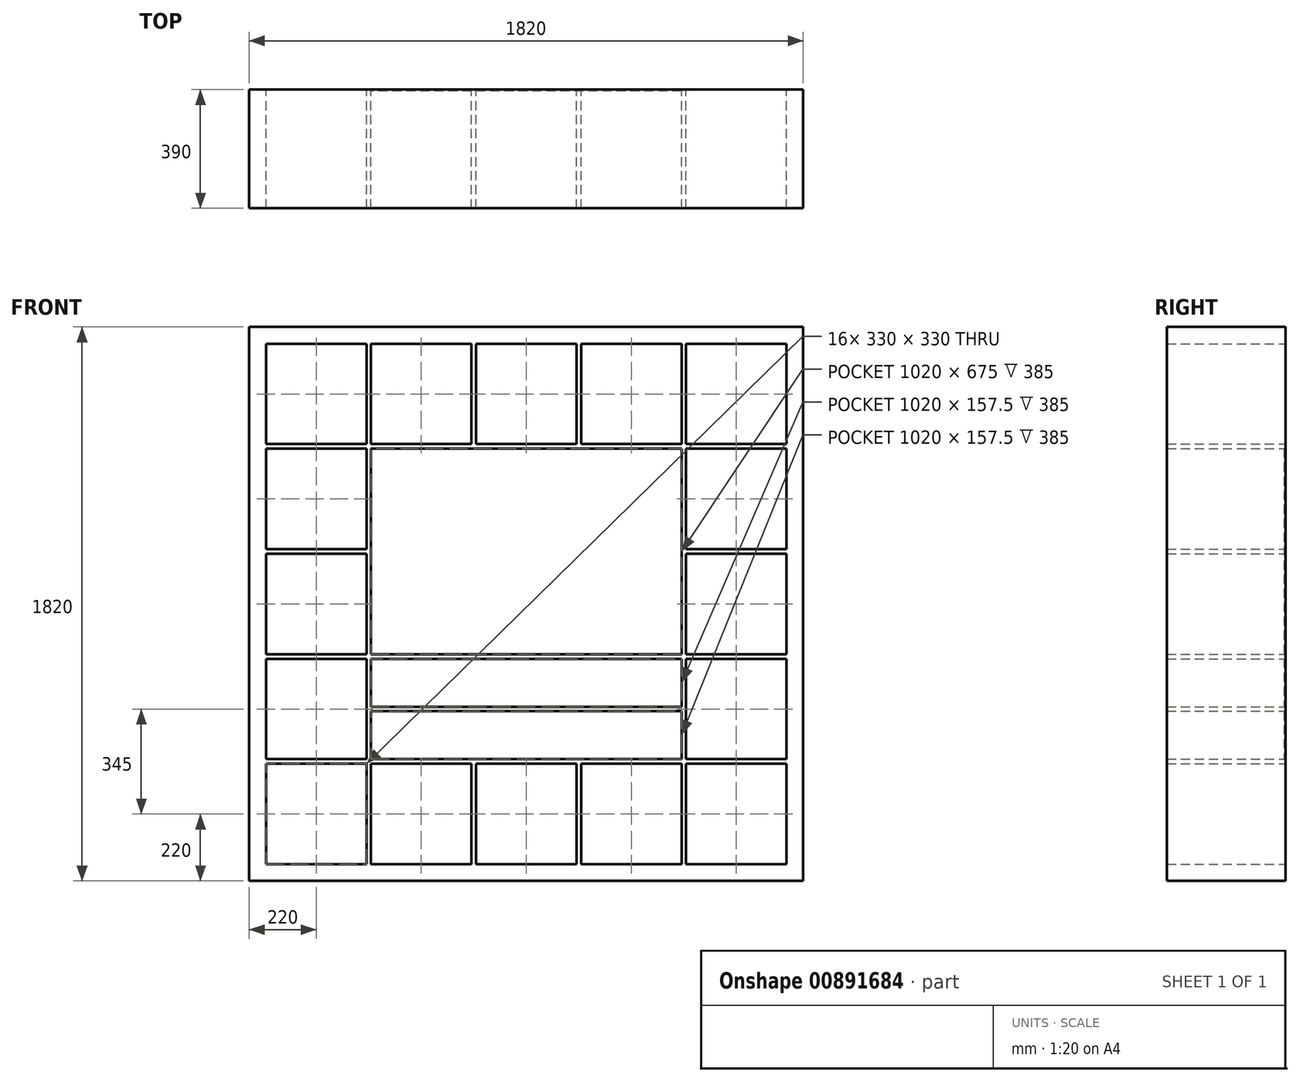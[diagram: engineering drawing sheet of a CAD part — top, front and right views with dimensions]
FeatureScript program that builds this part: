
annotation { "Feature Type Name" : "Feature", "Feature Type Description" : "" }
export const myFeature = defineFeature(function(context is Context, id is Id, definition is map)
    precondition{}
    {
        {
            var Q0;
            Q0=qCreatedBy(makeId("Front.planeOp"),FACE);
            var sketch = newSketch(context, id + "F0", { "sketchPlane" : qUnion([Q0])});
            skLineSegment(sketch, "E0.bottom", {"start": v(0, 1820) * mm, "end": v(1820, 1820) * mm});
            skLineSegment(sketch, "E0.top", {"start": v(0, 0) * mm, "end": v(1820, 0) * mm});
            skLineSegment(sketch, "E0.left", {"start": v(0, 1820) * mm, "end": v(0, 0) * mm});
            skLineSegment(sketch, "E0.right", {"start": v(1820, 1820) * mm, "end": v(1820, 0) * mm});
            skSolve(sketch);
        }
        {
            var Q0;
            Q0=makeQuery(id+"F0.imprint","IMPRINT",FACE,{"disambiguationData":[TD([[makeQuery(id+"F0.imprint","IMPRINT",EDGE,{"derivedFrom":sQuery(id+"F0.wireOp",EDGE,"E0.bottom")}),-1.0]])]});
            extrude(context, id + "F1", {"entities" : qUnion([Q0]), "depth" : 390 * mm});
        }
        {
            var Q0;
            Q0=qCreatedBy(makeId("Front.planeOp"),FACE);
            var sketch = newSketch(context, id + "F2", { "sketchPlane" : qUnion([Q0])});
            skLineSegment(sketch, "E1.bottom", {"start": v(385, 385) * mm, "end": v(55, 385) * mm});
            skLineSegment(sketch, "E1.top", {"start": v(385, 55) * mm, "end": v(55, 55) * mm});
            skLineSegment(sketch, "E1.left", {"start": v(385, 385) * mm, "end": v(385, 55) * mm});
            skLineSegment(sketch, "E1.right", {"start": v(55, 385) * mm, "end": v(55, 55) * mm});
            skLineSegment(sketch, "E2.0.1.0", {"start": v(385, 730) * mm, "end": v(385, 400) * mm});
            skLineSegment(sketch, "E2.0.1.1", {"start": v(385, 400) * mm, "end": v(55, 400) * mm});
            skLineSegment(sketch, "E2.0.1.2", {"start": v(55, 730) * mm, "end": v(55, 400) * mm});
            skLineSegment(sketch, "E2.0.1.3", {"start": v(385, 730) * mm, "end": v(55, 730) * mm});
            skLineSegment(sketch, "E2.0.2.0", {"start": v(385, 1075) * mm, "end": v(385, 745) * mm});
            skLineSegment(sketch, "E2.0.2.1", {"start": v(385, 745) * mm, "end": v(55, 745) * mm});
            skLineSegment(sketch, "E2.0.2.2", {"start": v(55, 1075) * mm, "end": v(55, 745) * mm});
            skLineSegment(sketch, "E2.0.2.3", {"start": v(385, 1075) * mm, "end": v(55, 1075) * mm});
            skLineSegment(sketch, "E2.0.3.0", {"start": v(385, 1420) * mm, "end": v(385, 1090) * mm});
            skLineSegment(sketch, "E2.0.3.1", {"start": v(385, 1090) * mm, "end": v(55, 1090) * mm});
            skLineSegment(sketch, "E2.0.3.2", {"start": v(55, 1420) * mm, "end": v(55, 1090) * mm});
            skLineSegment(sketch, "E2.0.3.3", {"start": v(385, 1420) * mm, "end": v(55, 1420) * mm});
            skLineSegment(sketch, "E2.0.4.0", {"start": v(385, 1765) * mm, "end": v(385, 1435) * mm});
            skLineSegment(sketch, "E2.0.4.1", {"start": v(385, 1435) * mm, "end": v(55, 1435) * mm});
            skLineSegment(sketch, "E2.0.4.2", {"start": v(55, 1765) * mm, "end": v(55, 1435) * mm});
            skLineSegment(sketch, "E2.0.4.3", {"start": v(385, 1765) * mm, "end": v(55, 1765) * mm});
            skLineSegment(sketch, "E2.1.0.0", {"start": v(730, 385) * mm, "end": v(730, 55) * mm});
            skLineSegment(sketch, "E2.1.0.1", {"start": v(730, 55) * mm, "end": v(400, 55) * mm});
            skLineSegment(sketch, "E2.1.0.2", {"start": v(400, 385) * mm, "end": v(400, 55) * mm});
            skLineSegment(sketch, "E2.1.0.3", {"start": v(730, 385) * mm, "end": v(400, 385) * mm});
            skLineSegment(sketch, "E2.1.1.0", {"start": v(730, 730) * mm, "end": v(730, 400) * mm});
            skLineSegment(sketch, "E2.1.1.1", {"start": v(730, 400) * mm, "end": v(400, 400) * mm});
            skLineSegment(sketch, "E2.1.1.2", {"start": v(400, 730) * mm, "end": v(400, 400) * mm});
            skLineSegment(sketch, "E2.1.1.3", {"start": v(730, 730) * mm, "end": v(400, 730) * mm});
            skLineSegment(sketch, "E2.1.2.0", {"start": v(730, 1075) * mm, "end": v(730, 745) * mm});
            skLineSegment(sketch, "E2.1.2.1", {"start": v(730, 745) * mm, "end": v(400, 745) * mm});
            skLineSegment(sketch, "E2.1.2.2", {"start": v(400, 1075) * mm, "end": v(400, 745) * mm});
            skLineSegment(sketch, "E2.1.2.3", {"start": v(730, 1075) * mm, "end": v(400, 1075) * mm});
            skLineSegment(sketch, "E2.1.3.0", {"start": v(730, 1420) * mm, "end": v(730, 1090) * mm});
            skLineSegment(sketch, "E2.1.3.1", {"start": v(730, 1090) * mm, "end": v(400, 1090) * mm});
            skLineSegment(sketch, "E2.1.3.2", {"start": v(400, 1420) * mm, "end": v(400, 1090) * mm});
            skLineSegment(sketch, "E2.1.3.3", {"start": v(730, 1420) * mm, "end": v(400, 1420) * mm});
            skLineSegment(sketch, "E2.1.4.0", {"start": v(730, 1765) * mm, "end": v(730, 1435) * mm});
            skLineSegment(sketch, "E2.1.4.1", {"start": v(730, 1435) * mm, "end": v(400, 1435) * mm});
            skLineSegment(sketch, "E2.1.4.2", {"start": v(400, 1765) * mm, "end": v(400, 1435) * mm});
            skLineSegment(sketch, "E2.1.4.3", {"start": v(730, 1765) * mm, "end": v(400, 1765) * mm});
            skLineSegment(sketch, "E2.2.0.0", {"start": v(1075, 385) * mm, "end": v(1075, 55) * mm});
            skLineSegment(sketch, "E2.2.0.1", {"start": v(1075, 55) * mm, "end": v(745, 55) * mm});
            skLineSegment(sketch, "E2.2.0.2", {"start": v(745, 385) * mm, "end": v(745, 55) * mm});
            skLineSegment(sketch, "E2.2.0.3", {"start": v(1075, 385) * mm, "end": v(745, 385) * mm});
            skLineSegment(sketch, "E2.2.1.0", {"start": v(1075, 730) * mm, "end": v(1075, 400) * mm});
            skLineSegment(sketch, "E2.2.1.1", {"start": v(1075, 400) * mm, "end": v(745, 400) * mm});
            skLineSegment(sketch, "E2.2.1.2", {"start": v(745, 730) * mm, "end": v(745, 400) * mm});
            skLineSegment(sketch, "E2.2.1.3", {"start": v(1075, 730) * mm, "end": v(745, 730) * mm});
            skLineSegment(sketch, "E2.2.2.0", {"start": v(1075, 1075) * mm, "end": v(1075, 745) * mm});
            skLineSegment(sketch, "E2.2.2.1", {"start": v(1075, 745) * mm, "end": v(745, 745) * mm});
            skLineSegment(sketch, "E2.2.2.2", {"start": v(745, 1075) * mm, "end": v(745, 745) * mm});
            skLineSegment(sketch, "E2.2.2.3", {"start": v(1075, 1075) * mm, "end": v(745, 1075) * mm});
            skLineSegment(sketch, "E2.2.3.0", {"start": v(1075, 1420) * mm, "end": v(1075, 1090) * mm});
            skLineSegment(sketch, "E2.2.3.1", {"start": v(1075, 1090) * mm, "end": v(745, 1090) * mm});
            skLineSegment(sketch, "E2.2.3.2", {"start": v(745, 1420) * mm, "end": v(745, 1090) * mm});
            skLineSegment(sketch, "E2.2.3.3", {"start": v(1075, 1420) * mm, "end": v(745, 1420) * mm});
            skLineSegment(sketch, "E2.2.4.0", {"start": v(1075, 1765) * mm, "end": v(1075, 1435) * mm});
            skLineSegment(sketch, "E2.2.4.1", {"start": v(1075, 1435) * mm, "end": v(745, 1435) * mm});
            skLineSegment(sketch, "E2.2.4.2", {"start": v(745, 1765) * mm, "end": v(745, 1435) * mm});
            skLineSegment(sketch, "E2.2.4.3", {"start": v(1075, 1765) * mm, "end": v(745, 1765) * mm});
            skLineSegment(sketch, "E2.3.0.0", {"start": v(1420, 385) * mm, "end": v(1420, 55) * mm});
            skLineSegment(sketch, "E2.3.0.1", {"start": v(1420, 55) * mm, "end": v(1090, 55) * mm});
            skLineSegment(sketch, "E2.3.0.2", {"start": v(1090, 385) * mm, "end": v(1090, 55) * mm});
            skLineSegment(sketch, "E2.3.0.3", {"start": v(1420, 385) * mm, "end": v(1090, 385) * mm});
            skLineSegment(sketch, "E2.3.1.0", {"start": v(1420, 730) * mm, "end": v(1420, 400) * mm});
            skLineSegment(sketch, "E2.3.1.1", {"start": v(1420, 400) * mm, "end": v(1090, 400) * mm});
            skLineSegment(sketch, "E2.3.1.2", {"start": v(1090, 730) * mm, "end": v(1090, 400) * mm});
            skLineSegment(sketch, "E2.3.1.3", {"start": v(1420, 730) * mm, "end": v(1090, 730) * mm});
            skLineSegment(sketch, "E2.3.2.0", {"start": v(1420, 1075) * mm, "end": v(1420, 745) * mm});
            skLineSegment(sketch, "E2.3.2.1", {"start": v(1420, 745) * mm, "end": v(1090, 745) * mm});
            skLineSegment(sketch, "E2.3.2.2", {"start": v(1090, 1075) * mm, "end": v(1090, 745) * mm});
            skLineSegment(sketch, "E2.3.2.3", {"start": v(1420, 1075) * mm, "end": v(1090, 1075) * mm});
            skLineSegment(sketch, "E2.3.3.0", {"start": v(1420, 1420) * mm, "end": v(1420, 1090) * mm});
            skLineSegment(sketch, "E2.3.3.1", {"start": v(1420, 1090) * mm, "end": v(1090, 1090) * mm});
            skLineSegment(sketch, "E2.3.3.2", {"start": v(1090, 1420) * mm, "end": v(1090, 1090) * mm});
            skLineSegment(sketch, "E2.3.3.3", {"start": v(1420, 1420) * mm, "end": v(1090, 1420) * mm});
            skLineSegment(sketch, "E2.3.4.0", {"start": v(1420, 1765) * mm, "end": v(1420, 1435) * mm});
            skLineSegment(sketch, "E2.3.4.1", {"start": v(1420, 1435) * mm, "end": v(1090, 1435) * mm});
            skLineSegment(sketch, "E2.3.4.2", {"start": v(1090, 1765) * mm, "end": v(1090, 1435) * mm});
            skLineSegment(sketch, "E2.3.4.3", {"start": v(1420, 1765) * mm, "end": v(1090, 1765) * mm});
            skLineSegment(sketch, "E2.4.0.0", {"start": v(1765, 385) * mm, "end": v(1765, 55) * mm});
            skLineSegment(sketch, "E2.4.0.1", {"start": v(1765, 55) * mm, "end": v(1435, 55) * mm});
            skLineSegment(sketch, "E2.4.0.2", {"start": v(1435, 385) * mm, "end": v(1435, 55) * mm});
            skLineSegment(sketch, "E2.4.0.3", {"start": v(1765, 385) * mm, "end": v(1435, 385) * mm});
            skLineSegment(sketch, "E2.4.1.0", {"start": v(1765, 730) * mm, "end": v(1765, 400) * mm});
            skLineSegment(sketch, "E2.4.1.1", {"start": v(1765, 400) * mm, "end": v(1435, 400) * mm});
            skLineSegment(sketch, "E2.4.1.2", {"start": v(1435, 730) * mm, "end": v(1435, 400) * mm});
            skLineSegment(sketch, "E2.4.1.3", {"start": v(1765, 730) * mm, "end": v(1435, 730) * mm});
            skLineSegment(sketch, "E2.4.2.0", {"start": v(1765, 1075) * mm, "end": v(1765, 745) * mm});
            skLineSegment(sketch, "E2.4.2.1", {"start": v(1765, 745) * mm, "end": v(1435, 745) * mm});
            skLineSegment(sketch, "E2.4.2.2", {"start": v(1435, 1075) * mm, "end": v(1435, 745) * mm});
            skLineSegment(sketch, "E2.4.2.3", {"start": v(1765, 1075) * mm, "end": v(1435, 1075) * mm});
            skLineSegment(sketch, "E2.4.3.0", {"start": v(1765, 1420) * mm, "end": v(1765, 1090) * mm});
            skLineSegment(sketch, "E2.4.3.1", {"start": v(1765, 1090) * mm, "end": v(1435, 1090) * mm});
            skLineSegment(sketch, "E2.4.3.2", {"start": v(1435, 1420) * mm, "end": v(1435, 1090) * mm});
            skLineSegment(sketch, "E2.4.3.3", {"start": v(1765, 1420) * mm, "end": v(1435, 1420) * mm});
            skLineSegment(sketch, "E2.4.4.0", {"start": v(1765, 1765) * mm, "end": v(1765, 1435) * mm});
            skLineSegment(sketch, "E2.4.4.1", {"start": v(1765, 1435) * mm, "end": v(1435, 1435) * mm});
            skLineSegment(sketch, "E2.4.4.2", {"start": v(1435, 1765) * mm, "end": v(1435, 1435) * mm});
            skLineSegment(sketch, "E2.4.4.3", {"start": v(1765, 1765) * mm, "end": v(1435, 1765) * mm});
            skLineSegment(sketch, "E2.direction1", {"start": v(385, 55) * mm, "end": v(730, 55) * mm, "construction": true});
            skLineSegment(sketch, "E2.direction2", {"start": v(385, 55) * mm, "end": v(385, 400) * mm, "construction": true});
            skLineSegment(sketch, "E3", {"start": v(730, 1420) * mm, "end": v(745, 1420) * mm});
            skLineSegment(sketch, "E4", {"start": v(1075, 1420) * mm, "end": v(1090, 1420) * mm});
            skLineSegment(sketch, "E5", {"start": v(1420, 1075) * mm, "end": v(1420, 1090) * mm});
            skLineSegment(sketch, "E6", {"start": v(1090, 745) * mm, "end": v(1075, 745) * mm});
            skLineSegment(sketch, "E7", {"start": v(745, 745) * mm, "end": v(730, 745) * mm});
            skLineSegment(sketch, "E8", {"start": v(400, 1075) * mm, "end": v(400, 1090) * mm});
            skLineSegment(sketch, "E9", {"start": v(400, 565) * mm, "end": v(1420, 565) * mm});
            skLineSegment(sketch, "E10", {"start": v(400, 572.5) * mm, "end": v(1420, 572.5) * mm});
            skLineSegment(sketch, "E11", {"start": v(400, 557.5) * mm, "end": v(1420, 557.5) * mm});
            skLineSegment(sketch, "E12", {"start": v(730, 730) * mm, "end": v(745, 730) * mm});
            skLineSegment(sketch, "E13", {"start": v(1075, 730) * mm, "end": v(1090, 730) * mm});
            skLineSegment(sketch, "E14", {"start": v(730, 400) * mm, "end": v(745, 400) * mm});
            skLineSegment(sketch, "E15", {"start": v(1075, 400) * mm, "end": v(1090, 400) * mm});
            skSolve(sketch);
        }
        {
            var Q0;
            Q0=makeQuery(id+"F2.imprint","IMPRINT",FACE,{"disambiguationData":[TD([[makeQuery(id+"F2.imprint","IMPRINT",EDGE,{"derivedFrom":sQuery(id+"F2.wireOp",EDGE,"E1.bottom")}),1.0]])]});
            var Q1;
            Q1=makeQuery(id+"F2.imprint","IMPRINT",FACE,{"disambiguationData":[TD([[makeQuery(id+"F2.imprint","IMPRINT",EDGE,{"derivedFrom":sQuery(id+"F2.wireOp",EDGE,"E2.0.1.0")}),-1.0]])]});
            var Q2;
            Q2=makeQuery(id+"F2.imprint","IMPRINT",FACE,{"disambiguationData":[TD([[makeQuery(id+"F2.imprint","IMPRINT",EDGE,{"derivedFrom":sQuery(id+"F2.wireOp",EDGE,"E2.0.2.0")}),-1.0]])]});
            var Q3;
            Q3=makeQuery(id+"F2.imprint","IMPRINT",FACE,{"disambiguationData":[TD([[makeQuery(id+"F2.imprint","IMPRINT",EDGE,{"derivedFrom":sQuery(id+"F2.wireOp",EDGE,"E2.0.3.0")}),-1.0]])]});
            var Q4;
            Q4=makeQuery(id+"F2.imprint","IMPRINT",FACE,{"disambiguationData":[TD([[makeQuery(id+"F2.imprint","IMPRINT",EDGE,{"derivedFrom":sQuery(id+"F2.wireOp",EDGE,"E2.0.4.0")}),-1.0]])]});
            var Q5;
            Q5=makeQuery(id+"F2.imprint","IMPRINT",FACE,{"disambiguationData":[TD([[makeQuery(id+"F2.imprint","IMPRINT",EDGE,{"derivedFrom":sQuery(id+"F2.wireOp",EDGE,"E2.1.0.0")}),-1.0]])]});
            var Q6;
            Q6=makeQuery(id+"F2.imprint","IMPRINT",FACE,{"disambiguationData":[TD([[makeQuery(id+"F2.imprint","IMPRINT",EDGE,{"derivedFrom":sQuery(id+"F2.wireOp",EDGE,"E2.1.4.0")}),-1.0]])]});
            var Q7;
            Q7=makeQuery(id+"F2.imprint","IMPRINT",FACE,{"disambiguationData":[TD([[makeQuery(id+"F2.imprint","IMPRINT",EDGE,{"derivedFrom":sQuery(id+"F2.wireOp",EDGE,"E2.2.0.0")}),-1.0]])]});
            var Q8;
            Q8=makeQuery(id+"F2.imprint","IMPRINT",FACE,{"disambiguationData":[TD([[makeQuery(id+"F2.imprint","IMPRINT",EDGE,{"derivedFrom":sQuery(id+"F2.wireOp",EDGE,"E2.2.4.0")}),-1.0]])]});
            var Q9;
            Q9=makeQuery(id+"F2.imprint","IMPRINT",FACE,{"disambiguationData":[TD([[makeQuery(id+"F2.imprint","IMPRINT",EDGE,{"derivedFrom":sQuery(id+"F2.wireOp",EDGE,"E2.3.0.0")}),-1.0]])]});
            var Q10;
            Q10=makeQuery(id+"F2.imprint","IMPRINT",FACE,{"disambiguationData":[TD([[makeQuery(id+"F2.imprint","IMPRINT",EDGE,{"derivedFrom":sQuery(id+"F2.wireOp",EDGE,"E2.3.4.0")}),-1.0]])]});
            var Q11;
            Q11=makeQuery(id+"F2.imprint","IMPRINT",FACE,{"disambiguationData":[TD([[makeQuery(id+"F2.imprint","IMPRINT",EDGE,{"derivedFrom":sQuery(id+"F2.wireOp",EDGE,"E2.4.0.0")}),-1.0]])]});
            var Q12;
            Q12=makeQuery(id+"F2.imprint","IMPRINT",FACE,{"disambiguationData":[TD([[makeQuery(id+"F2.imprint","IMPRINT",EDGE,{"derivedFrom":sQuery(id+"F2.wireOp",EDGE,"E2.4.1.0")}),-1.0]])]});
            var Q13;
            Q13=makeQuery(id+"F2.imprint","IMPRINT",FACE,{"disambiguationData":[TD([[makeQuery(id+"F2.imprint","IMPRINT",EDGE,{"derivedFrom":sQuery(id+"F2.wireOp",EDGE,"E2.4.2.0")}),-1.0]])]});
            var Q14;
            Q14=makeQuery(id+"F2.imprint","IMPRINT",FACE,{"disambiguationData":[TD([[makeQuery(id+"F2.imprint","IMPRINT",EDGE,{"derivedFrom":sQuery(id+"F2.wireOp",EDGE,"E2.4.3.0")}),-1.0]])]});
            var Q15;
            Q15=makeQuery(id+"F2.imprint","IMPRINT",FACE,{"disambiguationData":[TD([[makeQuery(id+"F2.imprint","IMPRINT",EDGE,{"derivedFrom":sQuery(id+"F2.wireOp",EDGE,"E2.4.4.0")}),-1.0]])]});
            var Q16;
            Q16=makeQuery(id+"F2.imprint","IMPRINT",FACE,{"disambiguationData":[TD([[makeQuery(id+"F2.imprint","IMPRINT",EDGE,{"derivedFrom":sQuery(id+"F2.wireOp",EDGE,"E2.1.2.0")}),-1.0]])]});
            var Q17;
            Q17=makeQuery(id+"F2.imprint","IMPRINT",FACE,{"disambiguationData":[TD([[makeQuery(id+"F2.imprint","IMPRINT",EDGE,{"derivedFrom":sQuery(id+"F2.wireOp",EDGE,"E2.1.3.0")}),-1.0]])]});
            var Q18;
            Q18=makeQuery(id+"F2.imprint","IMPRINT",FACE,{"disambiguationData":[TD([[makeQuery(id+"F2.imprint","IMPRINT",EDGE,{"derivedFrom":sQuery(id+"F2.wireOp",EDGE,"E2.2.2.0")}),-1.0]])]});
            var Q19;
            Q19=makeQuery(id+"F2.imprint","IMPRINT",FACE,{"disambiguationData":[TD([[makeQuery(id+"F2.imprint","IMPRINT",EDGE,{"derivedFrom":sQuery(id+"F2.wireOp",EDGE,"E2.2.3.0")}),-1.0]])]});
            var Q20;
            Q20=makeQuery(id+"F2.imprint","IMPRINT",FACE,{"disambiguationData":[TD([[makeQuery(id+"F2.imprint","IMPRINT",EDGE,{"derivedFrom":sQuery(id+"F2.wireOp",EDGE,"E2.3.2.0")}),-1.0]])]});
            var Q21;
            Q21=makeQuery(id+"F2.imprint","IMPRINT",FACE,{"disambiguationData":[TD([[makeQuery(id+"F2.imprint","IMPRINT",EDGE,{"derivedFrom":sQuery(id+"F2.wireOp",EDGE,"E2.3.3.0")}),-1.0]])]});
            var Q22;
            {var subQ0=sQuery(id+"F2.wireOp",EDGE,"E2.1.1.3");Q22=makeQuery(id+"F2.imprint","IMPRINT",FACE,{"disambiguationData":[TD([[makeQuery(id+"F2.imprint","IMPRINT",EDGE,{"derivedFrom":subQ0}),1.0]])]});}
            var Q23;
            {var subQ0=sQuery(id+"F2.wireOp",EDGE,"E2.1.1.1");Q23=makeQuery(id+"F2.imprint","IMPRINT",FACE,{"disambiguationData":[TD([[makeQuery(id+"F2.imprint","IMPRINT",EDGE,{"derivedFrom":subQ0}),-1.0]])]});}
            var Q24;
            {var subQ0=sQuery(id+"F2.wireOp",EDGE,"E2.3.1.3");Q24=makeQuery(id+"F2.imprint","IMPRINT",FACE,{"disambiguationData":[TD([[makeQuery(id+"F2.imprint","IMPRINT",EDGE,{"derivedFrom":subQ0}),1.0]])]});}
            var Q25;
            {var subQ0=sQuery(id+"F2.wireOp",EDGE,"E2.3.1.1");Q25=makeQuery(id+"F2.imprint","IMPRINT",FACE,{"disambiguationData":[TD([[makeQuery(id+"F2.imprint","IMPRINT",EDGE,{"derivedFrom":subQ0}),-1.0]])]});}
            var Q26;
            {var subQ0=sQuery(id+"F2.wireOp",EDGE,"E12");Q26=makeQuery(id+"F2.imprint","IMPRINT",FACE,{"disambiguationData":[TD([[makeQuery(id+"F2.imprint","IMPRINT",EDGE,{"derivedFrom":subQ0}),-1.0]])]});}
            var Q27;
            {var subQ0=sQuery(id+"F2.wireOp",EDGE,"E14");Q27=makeQuery(id+"F2.imprint","IMPRINT",FACE,{"disambiguationData":[TD([[makeQuery(id+"F2.imprint","IMPRINT",EDGE,{"derivedFrom":subQ0}),1.0]])]});}
            var Q28;
            {var subQ0=sQuery(id+"F2.wireOp",EDGE,"E2.2.1.3");Q28=makeQuery(id+"F2.imprint","IMPRINT",FACE,{"disambiguationData":[TD([[makeQuery(id+"F2.imprint","IMPRINT",EDGE,{"derivedFrom":subQ0}),1.0]])]});}
            var Q29;
            {var subQ0=sQuery(id+"F2.wireOp",EDGE,"E13");Q29=makeQuery(id+"F2.imprint","IMPRINT",FACE,{"disambiguationData":[TD([[makeQuery(id+"F2.imprint","IMPRINT",EDGE,{"derivedFrom":subQ0}),-1.0]])]});}
            var Q30;
            {var subQ0=sQuery(id+"F2.wireOp",EDGE,"E2.2.1.1");Q30=makeQuery(id+"F2.imprint","IMPRINT",FACE,{"disambiguationData":[TD([[makeQuery(id+"F2.imprint","IMPRINT",EDGE,{"derivedFrom":subQ0}),-1.0]])]});}
            var Q31;
            {var subQ0=sQuery(id+"F2.wireOp",EDGE,"E15");Q31=makeQuery(id+"F2.imprint","IMPRINT",FACE,{"disambiguationData":[TD([[makeQuery(id+"F2.imprint","IMPRINT",EDGE,{"derivedFrom":subQ0}),1.0]])]});}
            var Q32;
            Q32=makeQuery(id+"F2.imprint","IMPRINT",FACE,{"disambiguationData":[TD([[makeQuery(id+"F2.imprint","IMPRINT",EDGE,{"derivedFrom":sQuery(id+"F2.wireOp",EDGE,"E2.1.2.0")}),1.0]])]});
            extrude(context, id + "F3", {"entities" : qUnion([Q0, Q1, Q2, Q3, Q4, Q5, Q6, Q7, Q8, Q9, Q10, Q11, Q12, Q13, Q14, Q15, Q16, Q17, Q18, Q19, Q20, Q21, Q22, Q23, Q24, Q25, Q26, Q27, Q28, Q29, Q30, Q31, Q32]), "operationType" : NewBodyOperationType.REMOVE, "offsetDistance" : 25 * mm, "depth" : 740.6 * mm});
        }
        {
            var Q0;
            {var subQ0=sQuery(id+"F2.wireOp",EDGE,"E2.1.1.1");Q0=makeQuery(id+"F2.imprint","IMPRINT",FACE,{"disambiguationData":[TD([[makeQuery(id+"F2.imprint","IMPRINT",EDGE,{"derivedFrom":subQ0}),-1.0]])]});}
            var Q1;
            {var subQ0=sQuery(id+"F2.wireOp",EDGE,"E2.1.1.3");Q1=makeQuery(id+"F2.imprint","IMPRINT",FACE,{"disambiguationData":[TD([[makeQuery(id+"F2.imprint","IMPRINT",EDGE,{"derivedFrom":subQ0}),1.0]])]});}
            var Q2;
            {var subQ0=sQuery(id+"F2.wireOp",EDGE,"E2.2.1.3");Q2=makeQuery(id+"F2.imprint","IMPRINT",FACE,{"disambiguationData":[TD([[makeQuery(id+"F2.imprint","IMPRINT",EDGE,{"derivedFrom":subQ0}),1.0]])]});}
            var Q3;
            {var subQ0=sQuery(id+"F2.wireOp",EDGE,"E2.2.1.1");Q3=makeQuery(id+"F2.imprint","IMPRINT",FACE,{"disambiguationData":[TD([[makeQuery(id+"F2.imprint","IMPRINT",EDGE,{"derivedFrom":subQ0}),-1.0]])]});}
            var Q4;
            {var subQ0=sQuery(id+"F2.wireOp",EDGE,"E2.3.1.1");Q4=makeQuery(id+"F2.imprint","IMPRINT",FACE,{"disambiguationData":[TD([[makeQuery(id+"F2.imprint","IMPRINT",EDGE,{"derivedFrom":subQ0}),-1.0]])]});}
            var Q5;
            {var subQ0=sQuery(id+"F2.wireOp",EDGE,"E2.3.1.3");Q5=makeQuery(id+"F2.imprint","IMPRINT",FACE,{"disambiguationData":[TD([[makeQuery(id+"F2.imprint","IMPRINT",EDGE,{"derivedFrom":subQ0}),1.0]])]});}
            var Q6;
            Q6=makeQuery(id+"F2.imprint","IMPRINT",FACE,{"disambiguationData":[TD([[makeQuery(id+"F2.imprint","IMPRINT",EDGE,{"derivedFrom":sQuery(id+"F2.wireOp",EDGE,"E2.1.2.0")}),-1.0]])]});
            var Q7;
            Q7=makeQuery(id+"F2.imprint","IMPRINT",FACE,{"disambiguationData":[TD([[makeQuery(id+"F2.imprint","IMPRINT",EDGE,{"derivedFrom":sQuery(id+"F2.wireOp",EDGE,"E2.3.2.0")}),-1.0]])]});
            var Q8;
            Q8=makeQuery(id+"F2.imprint","IMPRINT",FACE,{"disambiguationData":[TD([[makeQuery(id+"F2.imprint","IMPRINT",EDGE,{"derivedFrom":sQuery(id+"F2.wireOp",EDGE,"E2.3.3.0")}),-1.0]])]});
            var Q9;
            Q9=makeQuery(id+"F2.imprint","IMPRINT",FACE,{"disambiguationData":[TD([[makeQuery(id+"F2.imprint","IMPRINT",EDGE,{"derivedFrom":sQuery(id+"F2.wireOp",EDGE,"E2.2.3.0")}),-1.0]])]});
            var Q10;
            Q10=makeQuery(id+"F2.imprint","IMPRINT",FACE,{"disambiguationData":[TD([[makeQuery(id+"F2.imprint","IMPRINT",EDGE,{"derivedFrom":sQuery(id+"F2.wireOp",EDGE,"E2.1.3.0")}),-1.0]])]});
            var Q11;
            Q11=makeQuery(id+"F2.imprint","IMPRINT",FACE,{"disambiguationData":[TD([[makeQuery(id+"F2.imprint","IMPRINT",EDGE,{"derivedFrom":sQuery(id+"F2.wireOp",EDGE,"E2.2.2.0")}),-1.0]])]});
            var Q12;
            Q12=makeQuery(id+"F2.imprint","IMPRINT",FACE,{"disambiguationData":[TD([[makeQuery(id+"F2.imprint","IMPRINT",EDGE,{"derivedFrom":sQuery(id+"F2.wireOp",EDGE,"E2.1.2.0")}),1.0]])]});
            var Q13;
            {var subQ0=sQuery(id+"F2.wireOp",EDGE,"E12");Q13=makeQuery(id+"F2.imprint","IMPRINT",FACE,{"disambiguationData":[TD([[makeQuery(id+"F2.imprint","IMPRINT",EDGE,{"derivedFrom":subQ0}),-1.0]])]});}
            var Q14;
            {var subQ0=sQuery(id+"F2.wireOp",EDGE,"E14");Q14=makeQuery(id+"F2.imprint","IMPRINT",FACE,{"disambiguationData":[TD([[makeQuery(id+"F2.imprint","IMPRINT",EDGE,{"derivedFrom":subQ0}),1.0]])]});}
            var Q15;
            {var subQ0=sQuery(id+"F2.wireOp",EDGE,"E15");Q15=makeQuery(id+"F2.imprint","IMPRINT",FACE,{"disambiguationData":[TD([[makeQuery(id+"F2.imprint","IMPRINT",EDGE,{"derivedFrom":subQ0}),1.0]])]});}
            var Q16;
            {var subQ0=sQuery(id+"F2.wireOp",EDGE,"E13");Q16=makeQuery(id+"F2.imprint","IMPRINT",FACE,{"disambiguationData":[TD([[makeQuery(id+"F2.imprint","IMPRINT",EDGE,{"derivedFrom":subQ0}),-1.0]])]});}
            extrude(context, id + "F4", {"entities" : qUnion([Q0, Q1, Q2, Q3, Q4, Q5, Q6, Q7, Q8, Q9, Q10, Q11, Q12, Q13, Q14, Q15, Q16]), "operationType" : NewBodyOperationType.ADD, "depth" : 5 * mm, "offsetDistance" : 25 * mm});
        }
    });
